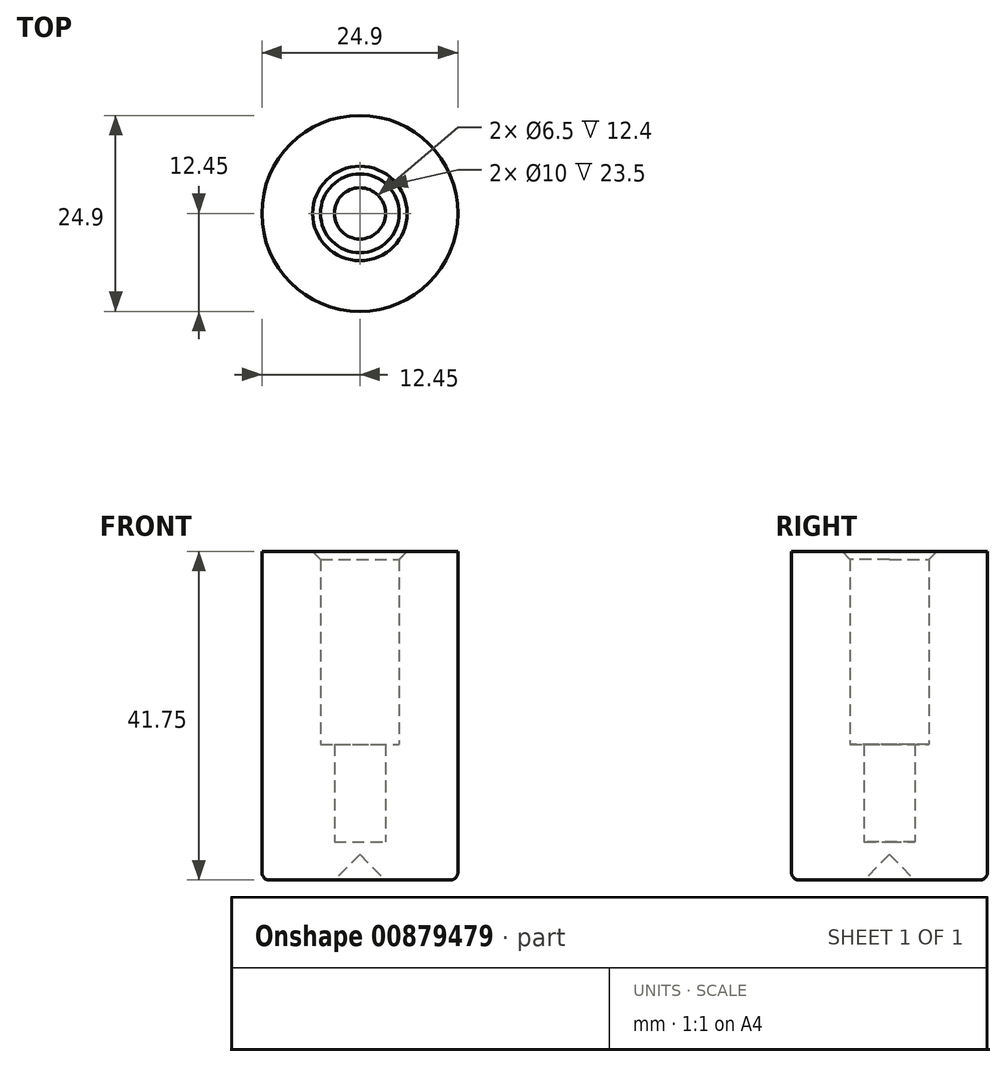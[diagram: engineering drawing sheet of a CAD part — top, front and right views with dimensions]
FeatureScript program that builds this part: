
annotation { "Feature Type Name" : "Feature", "Feature Type Description" : "" }
export const myFeature = defineFeature(function(context is Context, id is Id, definition is map)
    precondition{}
    {
        {
            var Q0;
            Q0=qCreatedBy(makeId("Front.planeOp"),FACE);
            var sketch = newSketch(context, id + "F0", { "sketchPlane" : qUnion([Q0])});
            skLineSegment(sketch, "E0", {"start": v(-12.45, 0) * mm, "end": v(-12.45, 41.75) * mm});
            skLineSegment(sketch, "E1", {"start": v(-12.45, 41.75) * mm, "end": v(-5, 41.75) * mm});
            skLineSegment(sketch, "E2", {"start": v(-3.25, 4.85) * mm, "end": v(0, 4.85) * mm});
            skLineSegment(sketch, "E3", {"start": v(-12.45, 0) * mm, "end": v(-3.25, 0) * mm});
            skLineSegment(sketch, "E4", {"start": v(-3.25, 0) * mm, "end": v(0, 3.25) * mm});
            skLineSegment(sketch, "E5", {"start": v(0, 3.25) * mm, "end": v(0, 4.85) * mm});
            skLineSegment(sketch, "E6", {"start": v(-3.25, 4.85) * mm, "end": v(-3.25, 17.25) * mm});
            skLineSegment(sketch, "E7", {"start": v(-5, 41.75) * mm, "end": v(-5, 17.25) * mm});
            skLineSegment(sketch, "E8", {"start": v(-5, 17.25) * mm, "end": v(-3.25, 17.25) * mm});
            skSolve(sketch);
        }
        {
            var Q0;
            Q0=makeQuery(id+"F0.imprint","IMPRINT",FACE,{"disambiguationData":[TD([[makeQuery(id+"F0.imprint","IMPRINT",EDGE,{"derivedFrom":sQuery(id+"F0.wireOp",EDGE,"E0")}),-1.0]])]});
            var Q1;
            Q1=sQuery(id+"F0.wireOp",EDGE,"E5");
            revolve(context, id + "F1", {"surfaceOperationType" : NewSurfaceOperationType.NEW, "entities" : qUnion([Q0]), "axis" : qUnion([Q1]), "revolveType" : RevolveType.FULL});
        }
        {
            var Q0;
            Q0=makeQuery(id+"F1.opRevolve","SWEPT_EDGE",EDGE,{"disambiguationData":[OSD([sQuery(id+"F0.wireOp",EDGE,"E1"),sQuery(id+"F0.wireOp",EDGE,"E7")])]});
            chamfer(context, id + "F2", {"entities" : qUnion([Q0]), "width" : 1 * mm, "tangentPropagation" : true});
        }
        {
            var Q0;
            Q0=makeQuery(id+"F1.opRevolve","SWEPT_EDGE",EDGE,{"disambiguationData":[OSD([sQuery(id+"F0.wireOp",EDGE,"E0"),sQuery(id+"F0.wireOp",EDGE,"E3")])]});
            fillet(context, id + "F3", {"entities" : qUnion([Q0]), "radius" : 1 * mm, "tangentPropagation" : true, "allowEdgeOverflow" : false});
        }
    });
